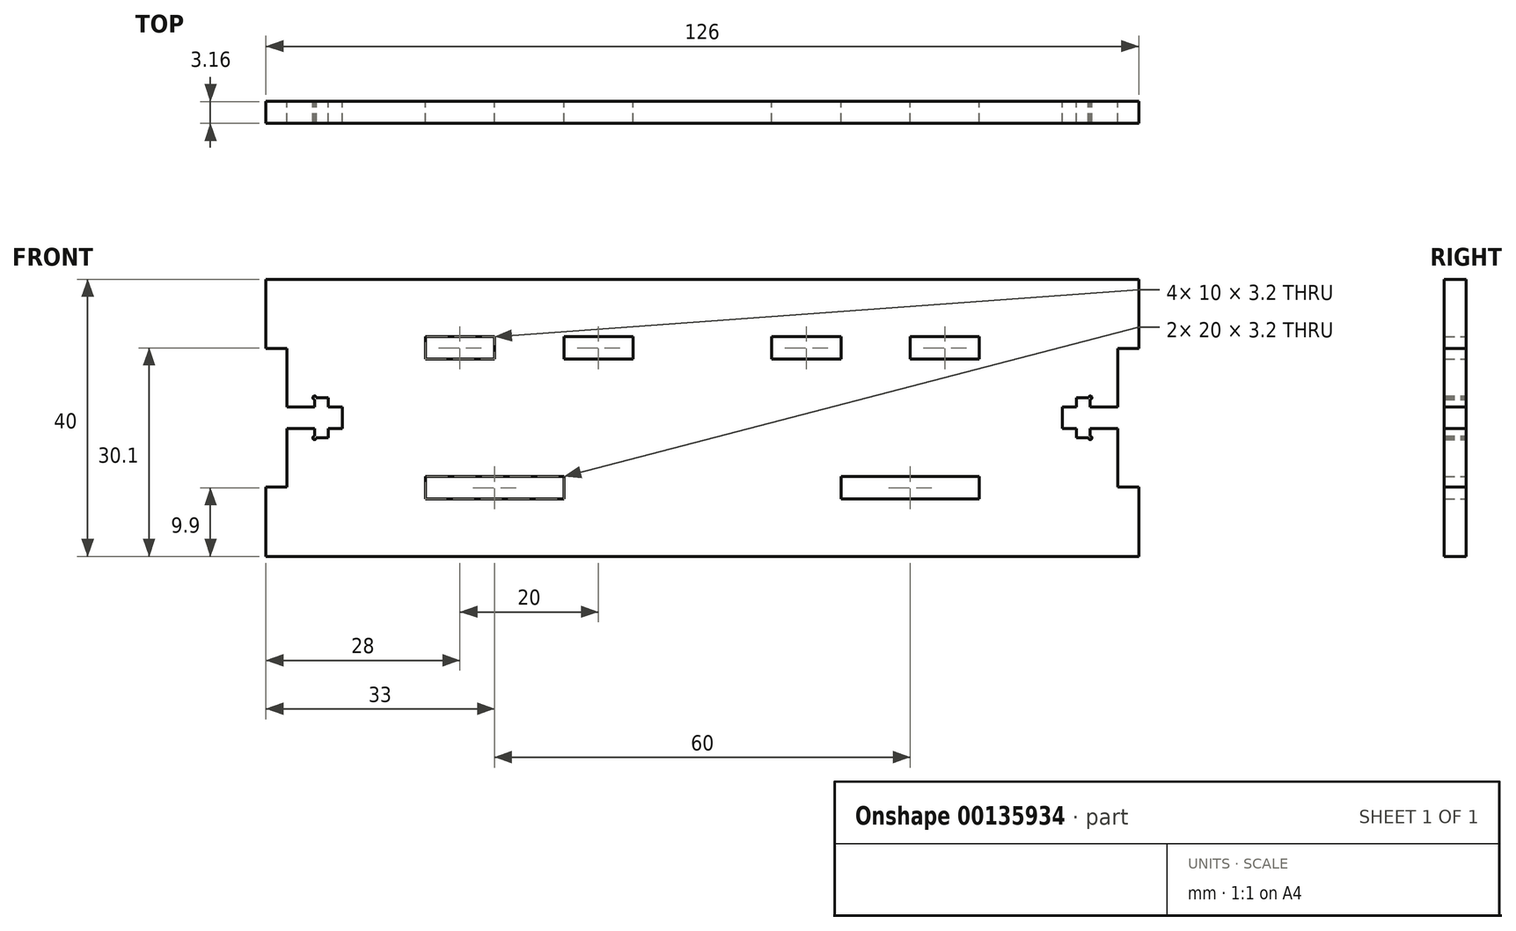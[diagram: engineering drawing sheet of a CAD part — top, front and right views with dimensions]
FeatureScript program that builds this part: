
annotation { "Feature Type Name" : "Feature", "Feature Type Description" : "" }
export const myFeature = defineFeature(function(context is Context, id is Id, definition is map)
    precondition{}
    {
        {
            var Q0;
            Q0=qCreatedBy(makeId("Front.planeOp"),FACE);
            var sketch = newSketch(context, id + "F0", { "sketchPlane" : qUnion([Q0])});
            skLineSegment(sketch, "E0", {"start": v(0, 20) * mm, "end": v(63, 20) * mm});
            skLineSegment(sketch, "E1", {"start": v(63, 20) * mm, "end": v(63, 10) * mm});
            skLineSegment(sketch, "E2", {"start": v(63, 10) * mm, "end": v(60, 10) * mm});
            skLineSegment(sketch, "E3", {"start": v(60, 10) * mm, "end": v(60, 1.55) * mm});
            skLineSegment(sketch, "E4", {"start": v(60, 1.55) * mm, "end": v(56, 1.55) * mm});
            skLineSegment(sketch, "E5", {"start": v(56, 1.55) * mm, "end": v(56, 2.9) * mm});
            skLineSegment(sketch, "E6", {"start": v(56, 2.9) * mm, "end": v(54, 2.9) * mm});
            skLineSegment(sketch, "E7", {"start": v(54, 2.9) * mm, "end": v(54, 1.55) * mm});
            skLineSegment(sketch, "E8", {"start": v(54, 1.55) * mm, "end": v(52, 1.55) * mm});
            skLineSegment(sketch, "E9", {"start": v(52, 1.55) * mm, "end": v(52, 0) * mm});
            skLineSegment(sketch, "E10.MirrorCS", {"start": v(56, -1.55) * mm, "end": v(56, -2.9) * mm});
            skLineSegment(sketch, "E11.MirrorCS", {"start": v(54, -2.9) * mm, "end": v(54, -1.55) * mm});
            skLineSegment(sketch, "E12.MirrorCS", {"start": v(52, -1.55) * mm, "end": v(52, 0) * mm});
            skLineSegment(sketch, "E13.MirrorCS", {"start": v(0, -20) * mm, "end": v(63, -20) * mm});
            skLineSegment(sketch, "E14.MirrorCS", {"start": v(63, -20) * mm, "end": v(63, -10) * mm});
            skLineSegment(sketch, "E15.MirrorCS", {"start": v(63, -10) * mm, "end": v(60, -10) * mm});
            skLineSegment(sketch, "E16.MirrorCS", {"start": v(60, -1.55) * mm, "end": v(56, -1.55) * mm});
            skLineSegment(sketch, "E17.MirrorCS", {"start": v(56, -2.9) * mm, "end": v(54, -2.9) * mm});
            skLineSegment(sketch, "E18.MirrorCS", {"start": v(54, -1.55) * mm, "end": v(52, -1.55) * mm});
            skLineSegment(sketch, "E19.MirrorCS", {"start": v(60, -10) * mm, "end": v(60, -1.55) * mm});
            skLineSegment(sketch, "E20.MirrorCS", {"start": v(-56, 1.55) * mm, "end": v(-56, 2.9) * mm});
            skLineSegment(sketch, "E21.MirrorCS", {"start": v(-54, 2.9) * mm, "end": v(-54, 1.55) * mm});
            skLineSegment(sketch, "E22.MirrorCS", {"start": v(-52, 1.55) * mm, "end": v(-52, 0) * mm});
            skLineSegment(sketch, "E23.MirrorCS", {"start": v(-56, -1.55) * mm, "end": v(-56, -2.9) * mm});
            skLineSegment(sketch, "E24.MirrorCS", {"start": v(-52, -1.55) * mm, "end": v(-52, 0) * mm});
            skLineSegment(sketch, "E25.MirrorCS", {"start": v(-54, -2.9) * mm, "end": v(-54, -1.55) * mm});
            skLineSegment(sketch, "E26.MirrorCS", {"start": v(-54, -1.55) * mm, "end": v(-52, -1.55) * mm});
            skLineSegment(sketch, "E27.MirrorCS", {"start": v(-60, 10) * mm, "end": v(-60, 1.55) * mm});
            skLineSegment(sketch, "E28.MirrorCS", {"start": v(-63, 10) * mm, "end": v(-60, 10) * mm});
            skLineSegment(sketch, "E29.MirrorCS", {"start": v(-56, 2.9) * mm, "end": v(-54, 2.9) * mm});
            skLineSegment(sketch, "E30.MirrorCS", {"start": v(-54, 1.55) * mm, "end": v(-52, 1.55) * mm});
            skLineSegment(sketch, "E31.MirrorCS", {"start": v(-60, -1.55) * mm, "end": v(-56, -1.55) * mm});
            skLineSegment(sketch, "E32.MirrorCS", {"start": v(-56, -2.9) * mm, "end": v(-54, -2.9) * mm});
            skLineSegment(sketch, "E33.MirrorCS", {"start": v(0, -20) * mm, "end": v(-63, -20) * mm});
            skLineSegment(sketch, "E34.MirrorCS", {"start": v(-60, 1.55) * mm, "end": v(-56, 1.55) * mm});
            skLineSegment(sketch, "E35.MirrorCS", {"start": v(-63, 20) * mm, "end": v(-63, 10) * mm});
            skLineSegment(sketch, "E36.MirrorCS", {"start": v(0, 20) * mm, "end": v(-63, 20) * mm});
            skLineSegment(sketch, "E37.MirrorCS", {"start": v(-60, -10) * mm, "end": v(-60, -1.55) * mm});
            skLineSegment(sketch, "E38.MirrorCS", {"start": v(-63, -20) * mm, "end": v(-63, -10) * mm});
            skLineSegment(sketch, "E39.MirrorCS", {"start": v(-63, -10) * mm, "end": v(-60, -10) * mm});
            skCircle(sketch, "E40", {"center": v(56, 2.9) * mm, "radius": 0.25 * mm});
            skCircle(sketch, "E41.MirrorC", {"center": v(56, -2.9) * mm, "radius": 0.25 * mm});
            skCircle(sketch, "E42.MirrorC", {"center": v(-56, -2.9) * mm, "radius": 0.25 * mm});
            skCircle(sketch, "E43.MirrorC", {"center": v(-56, 2.9) * mm, "radius": 0.25 * mm});
            skLineSegment(sketch, "E44.bottom", {"start": v(10, 11.7) * mm, "end": v(20, 11.7) * mm});
            skLineSegment(sketch, "E44.top", {"start": v(10, 8.5) * mm, "end": v(20, 8.5) * mm});
            skLineSegment(sketch, "E44.left", {"start": v(10, 11.7) * mm, "end": v(10, 8.5) * mm});
            skLineSegment(sketch, "E44.right", {"start": v(20, 11.7) * mm, "end": v(20, 8.5) * mm});
            skLineSegment(sketch, "E45.bottom", {"start": v(20, -8.5) * mm, "end": v(40, -8.5) * mm});
            skLineSegment(sketch, "E45.top", {"start": v(20, -11.7) * mm, "end": v(40, -11.7) * mm});
            skLineSegment(sketch, "E45.left", {"start": v(20, -8.5) * mm, "end": v(20, -11.7) * mm});
            skLineSegment(sketch, "E45.right", {"start": v(40, -8.5) * mm, "end": v(40, -11.7) * mm});
            skLineSegment(sketch, "E46.bottom", {"start": v(30, 11.7) * mm, "end": v(40, 11.7) * mm});
            skLineSegment(sketch, "E46.top", {"start": v(30, 8.5) * mm, "end": v(40, 8.5) * mm});
            skLineSegment(sketch, "E46.left", {"start": v(30, 11.7) * mm, "end": v(30, 8.5) * mm});
            skLineSegment(sketch, "E46.right", {"start": v(40, 11.7) * mm, "end": v(40, 8.5) * mm});
            skLineSegment(sketch, "E47.MirrorCS", {"start": v(-30, 11.7) * mm, "end": v(-30, 8.5) * mm});
            skLineSegment(sketch, "E48.MirrorCS", {"start": v(-40, 11.7) * mm, "end": v(-40, 8.5) * mm});
            skLineSegment(sketch, "E49.MirrorCS", {"start": v(-10, 11.7) * mm, "end": v(-10, 8.5) * mm});
            skLineSegment(sketch, "E50.MirrorCS", {"start": v(-20, 11.7) * mm, "end": v(-20, 8.5) * mm});
            skLineSegment(sketch, "E51.MirrorCS", {"start": v(-20, -8.5) * mm, "end": v(-20, -11.7) * mm});
            skLineSegment(sketch, "E52.MirrorCS", {"start": v(-40, -8.5) * mm, "end": v(-40, -11.7) * mm});
            skLineSegment(sketch, "E53.MirrorCS", {"start": v(-30, 11.7) * mm, "end": v(-40, 11.7) * mm});
            skLineSegment(sketch, "E54.MirrorCS", {"start": v(-10, 11.7) * mm, "end": v(-20, 11.7) * mm});
            skLineSegment(sketch, "E55.MirrorCS", {"start": v(-10, 8.5) * mm, "end": v(-20, 8.5) * mm});
            skLineSegment(sketch, "E56.MirrorCS", {"start": v(-30, 8.5) * mm, "end": v(-40, 8.5) * mm});
            skLineSegment(sketch, "E57.MirrorCS", {"start": v(-20, -11.7) * mm, "end": v(-40, -11.7) * mm});
            skLineSegment(sketch, "E58.MirrorCS", {"start": v(-20, -8.5) * mm, "end": v(-40, -8.5) * mm});
            skSolve(sketch);
        }
        {
            var Q0;
            Q0=makeQuery(id+"F0.imprint","IMPRINT",FACE,{"disambiguationData":[TD([[makeQuery(id+"F0.imprint","IMPRINT",EDGE,{"derivedFrom":sQuery(id+"F0.wireOp",EDGE,"E12.MirrorCS")}),1.0]])]});
            extrude(context, id + "F1", {"entities" : qUnion([Q0]), "depth" : 3.17 * mm, "symmetric" : true});
        }
    });
